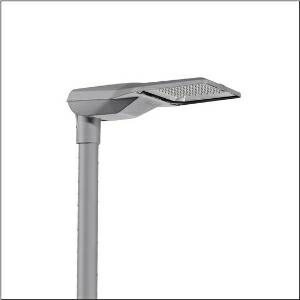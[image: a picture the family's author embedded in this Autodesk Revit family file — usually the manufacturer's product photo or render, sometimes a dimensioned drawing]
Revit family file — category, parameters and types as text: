
# Revit family: streetlight_sl_21_iq_midi___st0_8a_5xe3c41g08mb_fe6c
name_source: partatom
category: Lighting Fixtures
units: mm (PartAtom-declared; Revit-internal decimal feet)

## family parameters
Cut with Voids When Loaded = No
Host = Face
Light Source = No
Part Type = Normal
Room Calculation Point = No
Round Connector Dimension = Use Diameter
Shared = No

## types (1)
- --- (1 x LED, 20360 lm, 146.7 W, 4000K)
    Apparent Load = 147 VA
    CIE Flux Codes = 38 75 97 100 100
    Color Rendering = 70
    Color Temperature = 4000K
    Default Elevation = 1800 mm
    Description = Streetlight SL 21 iQ midi, mast luminaire, primary light control with lens, of PMMA, primary optical cover: cover, of toughened safety glass, transparent, light distribution: ST0.8a, light emission: direct distribution, primary light characteristic: asymmetric, installation type: post-top, side-entry, LED, High Power LED, rated luminous flux: 20.360lm, luminous efficacy: 139lm/W, light colour: 740, colour temperature: 4000K, control gear: iQ Street-Remote, control: Street-Remote, Auto-Match, Temp-Guard, Lumen-Switch, Night-Set, Smart-Wire, Light-Fading, Desk-Remote (wireless, voltage-free reading and setting of iQ features in the workshop via application-optimized NFC function/RFID function), optimised constant luminous flux control (CLO 2.0), pre-setting: linear dimming characteristic, mains connection: 230..240V, AC, 50/60Hz, start of lifetime: 147W, end of service life: 161W, reduction: 62W, luminaire housing, of diecast aluminium, powder-coated, SITECO metallic grey (DB 702S), corrosivity category C5 high according to DIN EN ISO 12944, please order mast flange separately, inclination adjustable: 0°, 5°, 10°, 15°, sealing non-destructively replaceable, multi-level sealing system, length: 644mm, width: 335mm, height: 110mm, mast flange for spigot size: 42mm (side-entry): 5XC10008XM4, 60/48mm (side-entry/post-top): 5XC10108XM2, 76/60mm (side-entry/post-top): 5XC10108XM1, mounting height: 4..8m, protection rating (complete): IP66, insulation class (complete): insulation class II (safety insulation), certification: CE, ENEC, ENEC+, VDE, impact resistance: IK10, permissible operating ambient temperature for outdoor applications: -40..+50°C, standard-compliant lighting for roads and squares, packaging unit: 1 piece

Light Distribution: ST0.8a
    Height = 111 mm
    Lamp = 1 x LED
    Lamp Light Flux = 20360 lm
    Lamp Power = 146.7 W
    Lamp count = 1
    Length = 644 mm
    Luminous efficacy = 139 lm/W
    Manufacturer = Siteco
    ModVariant = No
    Model = 5XE3C41G08MB
    Number of Poles = 1
    OnlyDefault = Yes
    Power Factor = 1
    Product Name = Streetlight SL 21 iQ midi | ST0.8a
    Product group = mast luminaire | pylon top
    ProductGroupID = 6100
    Protection Class = Protection class II
    Protection Degree = IP 66
    RLX_Detail_Level = 1
    RLX_Emergency_Light_Flux = 0 lm
    RLX_Emergency_Type = 0
    RLX_Emergency_Type_DB = No
    RlxData = <blob elided: 26985 chars, md5=57a91737>
    Socket = socket
    Standby Power = 0 W
    System Light Flux = 20360 lm
    System Power = 147 W
    Type Comments = factory setting: luminous flux: 100 % | dim-lin: 254 | 753 mA
    Type Image = l_1004298.jpg
    URL = http://relux.com
    VarID = @adj_183607
    Voltage = 0 V
    Weight = 0.00 kg
    Width = 336 mm

## geometry (parser evidence)
native form markers: Blend x4, Sweep x12
no freeform markers — native parametric forms only
